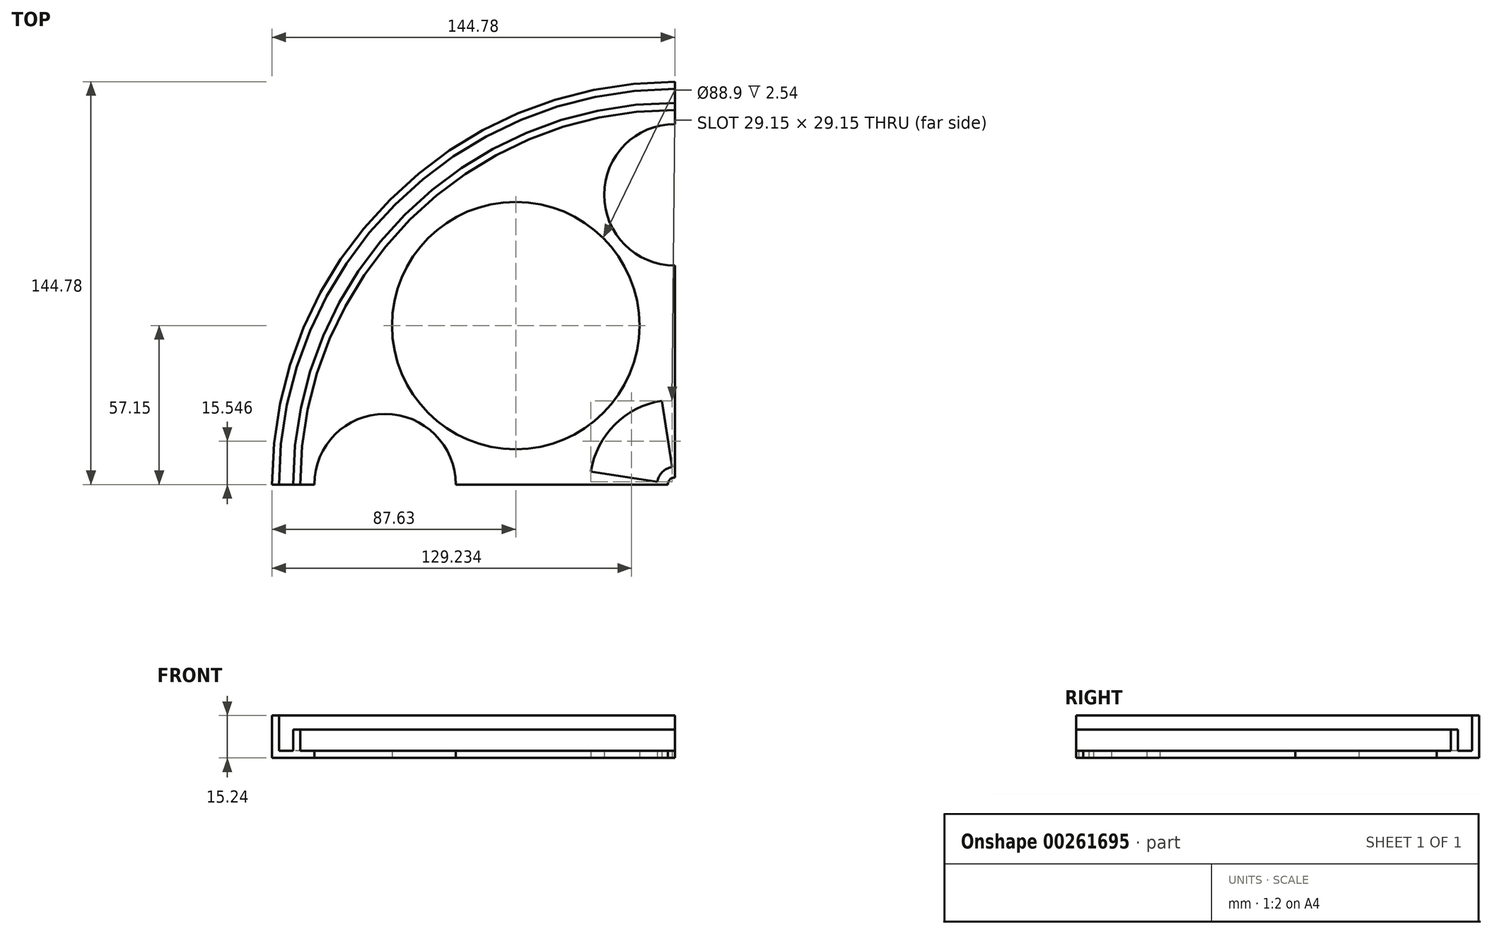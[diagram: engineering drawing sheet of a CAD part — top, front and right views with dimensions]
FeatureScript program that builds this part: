
annotation { "Feature Type Name" : "Feature", "Feature Type Description" : "" }
export const myFeature = defineFeature(function(context is Context, id is Id, definition is map)
    precondition{}
    {
        {
            var Q0;
            Q0=qCreatedBy(makeId("Top.planeOp"),FACE);
            var sketch = newSketch(context, id + "F0", { "sketchPlane" : qUnion([Q0])});
            skCircle(sketch, "E0", {"center": v(0, 0) * mm, "radius": 134.62 * mm});
            skCircle(sketch, "E1.0", {"center": v(0, 0) * mm, "radius": 137.16 * mm});
            skCircle(sketch, "E2.0", {"center": v(0, 0) * mm, "radius": 144.78 * mm});
            skCircle(sketch, "E3.0", {"center": v(0, 0) * mm, "radius": 142.24 * mm});
            skCircle(sketch, "E4.0", {"center": v(0, 0) * mm, "radius": 2.54 * mm});
            skLineSegment(sketch, "E5", {"start": v(0, 0) * mm, "end": v(0, -147.32) * mm});
            skLineSegment(sketch, "E6", {"start": v(-11.57, -144.32) * mm, "end": v(0, -147.32) * mm});
            skFitSpline(sketch, "E7", {"points": [v(0, -147.32) * mm, v(5.92, -144.66) * mm], "startDerivative": vector(10.02, -2.47) * mm, "endDerivative": vector(12.8, 0.33) * mm});
            skLineSegment(sketch, "E8", {"start": v(-8.6, -141.98) * mm, "end": v(0, -144.78) * mm});
            skFitSpline(sketch, "E9", {"points": [v(0, -144.78) * mm, v(4.46, -142.17) * mm], "startDerivative": vector(6.28, -2.02) * mm, "endDerivative": vector(5.88, 0.14) * mm});
            skLineSegment(sketch, "E10", {"start": v(0, 0) * mm, "end": v(-144.78, 0) * mm});
            skLineSegment(sketch, "E11", {"start": v(0, 0) * mm, "end": v(0, 144.78) * mm});
            skLineSegment(sketch, "E12", {"start": v(0, 0) * mm, "end": v(144.78, 0) * mm});
            skLineSegment(sketch, "E13", {"start": v(0, -12.7) * mm, "end": v(-144.22, -12.7) * mm});
            skLineSegment(sketch, "E14", {"start": v(0, -12.7) * mm, "end": v(144.78, -12.7) * mm});
            skLineSegment(sketch, "E15", {"start": v(0, 12.7) * mm, "end": v(-144.22, 12.7) * mm});
            skLineSegment(sketch, "E16", {"start": v(0, 12.7) * mm, "end": v(144.78, 12.7) * mm});
            skLineSegment(sketch, "E17", {"start": v(-12.7, 0) * mm, "end": v(-12.7, 144.22) * mm});
            skLineSegment(sketch, "E18", {"start": v(12.7, 0) * mm, "end": v(12.7, 144.22) * mm});
            skLineSegment(sketch, "E19", {"start": v(-12.7, 0) * mm, "end": v(-12.7, -144.22) * mm});
            skLineSegment(sketch, "E20", {"start": v(12.7, 0) * mm, "end": v(12.7, -144.22) * mm});
            skCircle(sketch, "E21", {"center": v(-57.15, -57.15) * mm, "radius": 44.45 * mm});
            skCircle(sketch, "E22", {"center": v(57.15, -57.15) * mm, "radius": 44.45 * mm});
            skCircle(sketch, "E23", {"center": v(-57.15, 57.15) * mm, "radius": 44.45 * mm});
            skCircle(sketch, "E24", {"center": v(57.15, 57.15) * mm, "radius": 44.45 * mm});
            skCircle(sketch, "E25", {"center": v(-104.14, 0) * mm, "radius": 25.4 * mm});
            skCircle(sketch, "E26", {"center": v(0, 104.14) * mm, "radius": 25.4 * mm});
            skCircle(sketch, "E27", {"center": v(104.14, 0) * mm, "radius": 25.4 * mm});
            skCircle(sketch, "E28", {"center": v(0, -104.14) * mm, "radius": 25.4 * mm});
            skCircle(sketch, "E29", {"center": v(0, 0) * mm, "radius": 30.48 * mm});
            skLineSegment(sketch, "E30", {"start": v(-12.7, -82.14) * mm, "end": v(0, 0) * mm});
            skLineSegment(sketch, "E31", {"start": v(12.7, -82.14) * mm, "end": v(0, 0) * mm});
            skLineSegment(sketch, "E32", {"start": v(82.14, -12.7) * mm, "end": v(0, 0) * mm});
            skLineSegment(sketch, "E33", {"start": v(82.14, 12.7) * mm, "end": v(0, 0) * mm});
            skLineSegment(sketch, "E34", {"start": v(12.7, 82.14) * mm, "end": v(0, 0) * mm});
            skLineSegment(sketch, "E35", {"start": v(-12.7, 82.14) * mm, "end": v(0, 0) * mm});
            skLineSegment(sketch, "E36", {"start": v(-82.14, -12.7) * mm, "end": v(0, 0) * mm});
            skLineSegment(sketch, "E37", {"start": v(-82.14, 12.7) * mm, "end": v(0, 0) * mm});
            skCircle(sketch, "E38", {"center": v(0, 0) * mm, "radius": 6.35 * mm});
            skSolve(sketch);
        }
        {
            var Q0;
            {var subQ0=sQuery(id+"F0.wireOp",EDGE,"E17");var subQ5=sQuery(id+"F0.wireOp",EDGE,"E37");var subQ7=makeQuery(id+"F0.imprint","INTERSECT",VERTEX,{"derivedFrom":[subQ0,subQ5]});Q0=makeQuery(id+"F0.imprint","IMPRINT",FACE,{"disambiguationData":[TD([[makeQuery(id+"F0.imprint","IMPRINT",EDGE,{"disambiguationData":[TD([[subQ7,-1.0]])],"derivedFrom":subQ5}),-1.0]])]});}
            var Q1;
            {var subQ0=sQuery(id+"F0.wireOp",EDGE,"E37");var subQ1=sQuery(id+"F0.wireOp",EDGE,"E4.0");var subQ2=makeQuery(id+"F0.imprint","INTERSECT",VERTEX,{"derivedFrom":[subQ1,subQ0]});Q1=makeQuery(id+"F0.imprint","IMPRINT",FACE,{"disambiguationData":[TD([[makeQuery(id+"F0.imprint","IMPRINT",EDGE,{"disambiguationData":[TD([[subQ2,-1.0]])],"derivedFrom":subQ1}),-1.0]])]});}
            var Q2;
            {var subQ0=sQuery(id+"F0.wireOp",EDGE,"E35");var subQ1=sQuery(id+"F0.wireOp",EDGE,"E4.0");var subQ2=makeQuery(id+"F0.imprint","INTERSECT",VERTEX,{"derivedFrom":[subQ1,subQ0]});Q2=makeQuery(id+"F0.imprint","IMPRINT",FACE,{"disambiguationData":[TD([[makeQuery(id+"F0.imprint","IMPRINT",EDGE,{"disambiguationData":[TD([[subQ2,-1.0]])],"derivedFrom":subQ1}),-1.0]])]});}
            var Q3;
            {var subQ0=sQuery(id+"F0.wireOp",EDGE,"E11");var subQ1=sQuery(id+"F0.wireOp",EDGE,"E4.0");var subQ2=makeQuery(id+"F0.imprint","INTERSECT",VERTEX,{"derivedFrom":[subQ1,subQ0]});Q3=makeQuery(id+"F0.imprint","IMPRINT",FACE,{"disambiguationData":[TD([[makeQuery(id+"F0.imprint","IMPRINT",EDGE,{"disambiguationData":[TD([[subQ2,-1.0]])],"derivedFrom":subQ1}),-1.0]])]});}
            var Q4;
            {var subQ0=sQuery(id+"F0.wireOp",EDGE,"E15");var subQ5=sQuery(id+"F0.wireOp",EDGE,"E35");var subQ6=makeQuery(id+"F0.imprint","INTERSECT",VERTEX,{"derivedFrom":[subQ0,subQ5]});Q4=makeQuery(id+"F0.imprint","IMPRINT",FACE,{"disambiguationData":[TD([[makeQuery(id+"F0.imprint","IMPRINT",EDGE,{"disambiguationData":[TD([[subQ6,-1.0]])],"derivedFrom":subQ5}),1.0]])]});}
            var Q5;
            {var subQ1=sQuery(id+"F0.wireOp",EDGE,"E11");var subQ3=sQuery(id+"F0.wireOp",EDGE,"E29");var subQ4=makeQuery(id+"F0.imprint","INTERSECT",VERTEX,{"derivedFrom":[subQ1,subQ3]});Q5=makeQuery(id+"F0.imprint","IMPRINT",FACE,{"disambiguationData":[TD([[makeQuery(id+"F0.imprint","IMPRINT",EDGE,{"disambiguationData":[TD([[subQ4,-1.0]])],"derivedFrom":subQ3}),1.0]])]});}
            var Q6;
            {var subQ1=sQuery(id+"F0.wireOp",EDGE,"E10");var subQ3=sQuery(id+"F0.wireOp",EDGE,"E29");var subQ4=makeQuery(id+"F0.imprint","INTERSECT",VERTEX,{"derivedFrom":[subQ1,subQ3]});Q6=makeQuery(id+"F0.imprint","IMPRINT",FACE,{"disambiguationData":[TD([[makeQuery(id+"F0.imprint","IMPRINT",EDGE,{"disambiguationData":[TD([[subQ4,1.0]])],"derivedFrom":subQ3}),1.0]])]});}
            var Q7;
            {var subQ0=sQuery(id+"F0.wireOp",EDGE,"E29");var subQ1=sQuery(id+"F0.wireOp",EDGE,"E10");var subQ2=makeQuery(id+"F0.imprint","INTERSECT",VERTEX,{"derivedFrom":[subQ1,subQ0]});Q7=makeQuery(id+"F0.imprint","IMPRINT",FACE,{"disambiguationData":[TD([[makeQuery(id+"F0.imprint","IMPRINT",EDGE,{"disambiguationData":[TD([[subQ2,-1.0]])],"derivedFrom":subQ1}),-1.0]])]});}
            var Q8;
            {var subQ1=sQuery(id+"F0.wireOp",EDGE,"E17");var subQ9=sQuery(id+"F0.wireOp",EDGE,"E0");var subQ10=makeQuery(id+"F0.imprint","INTERSECT",VERTEX,{"derivedFrom":[subQ9,subQ1]});Q8=makeQuery(id+"F0.imprint","IMPRINT",FACE,{"disambiguationData":[TD([[makeQuery(id+"F0.imprint","IMPRINT",EDGE,{"disambiguationData":[TD([[subQ10,-1.0]])],"derivedFrom":subQ9}),1.0]])]});}
            var Q9;
            {var subQ0=sQuery(id+"F0.wireOp",EDGE,"E15");var subQ1=sQuery(id+"F0.wireOp",EDGE,"E0");var subQ2=makeQuery(id+"F0.imprint","INTERSECT",VERTEX,{"derivedFrom":[subQ1,subQ0]});Q9=makeQuery(id+"F0.imprint","IMPRINT",FACE,{"disambiguationData":[TD([[makeQuery(id+"F0.imprint","IMPRINT",EDGE,{"disambiguationData":[TD([[subQ2,-1.0]])],"derivedFrom":subQ1}),1.0]])]});}
            var Q10;
            {var subQ0=sQuery(id+"F0.wireOp",EDGE,"E29");var subQ1=sQuery(id+"F0.wireOp",EDGE,"E15");var subQ2=makeQuery(id+"F0.imprint","INTERSECT",VERTEX,{"derivedFrom":[subQ1,subQ0]});Q10=makeQuery(id+"F0.imprint","IMPRINT",FACE,{"disambiguationData":[TD([[makeQuery(id+"F0.imprint","IMPRINT",EDGE,{"disambiguationData":[TD([[subQ2,-1.0]])],"derivedFrom":subQ1}),1.0]])]});}
            var Q11;
            {var subQ0=sQuery(id+"F0.wireOp",EDGE,"E29");var subQ1=sQuery(id+"F0.wireOp",EDGE,"E15");var subQ2=makeQuery(id+"F0.imprint","INTERSECT",VERTEX,{"derivedFrom":[subQ1,subQ0]});Q11=makeQuery(id+"F0.imprint","IMPRINT",FACE,{"disambiguationData":[TD([[makeQuery(id+"F0.imprint","IMPRINT",EDGE,{"disambiguationData":[TD([[subQ2,-1.0]])],"derivedFrom":subQ1}),-1.0]])]});}
            var Q12;
            {var subQ0=sQuery(id+"F0.wireOp",EDGE,"E29");var subQ1=sQuery(id+"F0.wireOp",EDGE,"E17");var subQ2=makeQuery(id+"F0.imprint","INTERSECT",VERTEX,{"derivedFrom":[subQ1,subQ0]});Q12=makeQuery(id+"F0.imprint","IMPRINT",FACE,{"disambiguationData":[TD([[makeQuery(id+"F0.imprint","IMPRINT",EDGE,{"disambiguationData":[TD([[subQ2,-1.0]])],"derivedFrom":subQ1}),-1.0]])]});}
            var Q13;
            {var subQ0=sQuery(id+"F0.wireOp",EDGE,"E29");var subQ1=sQuery(id+"F0.wireOp",EDGE,"E11");var subQ2=makeQuery(id+"F0.imprint","INTERSECT",VERTEX,{"derivedFrom":[subQ1,subQ0]});Q13=makeQuery(id+"F0.imprint","IMPRINT",FACE,{"disambiguationData":[TD([[makeQuery(id+"F0.imprint","IMPRINT",EDGE,{"disambiguationData":[TD([[subQ2,-1.0]])],"derivedFrom":subQ1}),1.0]])]});}
            var Q14;
            {var subQ0=sQuery(id+"F0.wireOp",EDGE,"E11");var subQ1=sQuery(id+"F0.wireOp",EDGE,"E0");var subQ2=makeQuery(id+"F0.imprint","INTERSECT",VERTEX,{"derivedFrom":[subQ1,subQ0]});Q14=makeQuery(id+"F0.imprint","IMPRINT",FACE,{"disambiguationData":[TD([[makeQuery(id+"F0.imprint","IMPRINT",EDGE,{"disambiguationData":[TD([[subQ2,-1.0]])],"derivedFrom":subQ1}),1.0]])]});}
            extrude(context, id + "F1", {"entities" : qUnion([Q0, Q1, Q2, Q3, Q4, Q5, Q6, Q7, Q8, Q9, Q10, Q11, Q12, Q13, Q14]), "offsetDistance" : 25.4 * mm, "depth" : 2.54 * mm});
        }
        {
            var Q0;
            {var subQ0=sQuery(id+"F0.wireOp",EDGE,"E15");var subQ1=sQuery(id+"F0.wireOp",EDGE,"E0");var subQ2=makeQuery(id+"F0.imprint","INTERSECT",VERTEX,{"derivedFrom":[subQ1,subQ0]});Q0=makeQuery(id+"F0.imprint","IMPRINT",FACE,{"disambiguationData":[TD([[makeQuery(id+"F0.imprint","IMPRINT",EDGE,{"disambiguationData":[TD([[subQ2,-1.0]])],"derivedFrom":subQ1}),-1.0]])]});}
            var Q1;
            {var subQ0=sQuery(id+"F0.wireOp",EDGE,"E17");var subQ1=sQuery(id+"F0.wireOp",EDGE,"E0");var subQ2=makeQuery(id+"F0.imprint","INTERSECT",VERTEX,{"derivedFrom":[subQ1,subQ0]});Q1=makeQuery(id+"F0.imprint","IMPRINT",FACE,{"disambiguationData":[TD([[makeQuery(id+"F0.imprint","IMPRINT",EDGE,{"disambiguationData":[TD([[subQ2,-1.0]])],"derivedFrom":subQ1}),-1.0]])]});}
            var Q2;
            {var subQ0=sQuery(id+"F0.wireOp",EDGE,"E11");var subQ1=sQuery(id+"F0.wireOp",EDGE,"E0");var subQ2=makeQuery(id+"F0.imprint","INTERSECT",VERTEX,{"derivedFrom":[subQ1,subQ0]});Q2=makeQuery(id+"F0.imprint","IMPRINT",FACE,{"disambiguationData":[TD([[makeQuery(id+"F0.imprint","IMPRINT",EDGE,{"disambiguationData":[TD([[subQ2,-1.0]])],"derivedFrom":subQ1}),-1.0]])]});}
            extrude(context, id + "F2", {"entities" : qUnion([Q0, Q1, Q2]), "operationType" : NewBodyOperationType.ADD, "offsetDistance" : 25.4 * mm, "depth" : 7.62 * mm});
        }
        {
            var Q0;
            {var subQ0=sQuery(id+"F0.wireOp",EDGE,"E15");var subQ1=sQuery(id+"F0.wireOp",EDGE,"E1.0");var subQ2=makeQuery(id+"F0.imprint","INTERSECT",VERTEX,{"derivedFrom":[subQ1,subQ0]});Q0=makeQuery(id+"F0.imprint","IMPRINT",FACE,{"disambiguationData":[TD([[makeQuery(id+"F0.imprint","IMPRINT",EDGE,{"disambiguationData":[TD([[subQ2,-1.0]])],"derivedFrom":subQ1}),-1.0]])]});}
            var Q1;
            {var subQ0=sQuery(id+"F0.wireOp",EDGE,"E17");var subQ1=sQuery(id+"F0.wireOp",EDGE,"E1.0");var subQ2=makeQuery(id+"F0.imprint","INTERSECT",VERTEX,{"derivedFrom":[subQ1,subQ0]});Q1=makeQuery(id+"F0.imprint","IMPRINT",FACE,{"disambiguationData":[TD([[makeQuery(id+"F0.imprint","IMPRINT",EDGE,{"disambiguationData":[TD([[subQ2,-1.0]])],"derivedFrom":subQ1}),-1.0]])]});}
            var Q2;
            Q2=makeQuery(id+"F2.opExtrude","CAP_FACE",FACE,{"disambiguationData":[OSD([sQuery(id+"F0.wireOp",EDGE,"E0"),sQuery(id+"F0.wireOp",EDGE,"E1.0"),sQuery(id+"F0.wireOp",EDGE,"E5"),sQuery(id+"F0.wireOp",EDGE,"E19")])],"isStart":false});
            var Q3;
            {var subQ0=sQuery(id+"F0.wireOp",EDGE,"E11");var subQ1=sQuery(id+"F0.wireOp",EDGE,"E1.0");var subQ2=makeQuery(id+"F0.imprint","INTERSECT",VERTEX,{"derivedFrom":[subQ1,subQ0]});Q3=makeQuery(id+"F0.imprint","IMPRINT",FACE,{"disambiguationData":[TD([[makeQuery(id+"F0.imprint","IMPRINT",EDGE,{"disambiguationData":[TD([[subQ2,-1.0]])],"derivedFrom":subQ1}),-1.0]])]});}
            extrude(context, id + "F3", {"entities" : qUnion([Q0, Q1, Q2, Q3]), "operationType" : NewBodyOperationType.ADD, "offsetDistance" : 25.4 * mm, "depth" : 2.54 * mm});
        }
        {
            var Q0;
            {var subQ0=sQuery(id+"F0.wireOp",EDGE,"E10");var subQ1=sQuery(id+"F0.wireOp",EDGE,"E2.0");var subQ2=makeQuery(id+"F0.imprint","INTERSECT",VERTEX,{"derivedFrom":[subQ1,subQ0]});Q0=makeQuery(id+"F0.imprint","IMPRINT",FACE,{"disambiguationData":[TD([[makeQuery(id+"F0.imprint","IMPRINT",EDGE,{"disambiguationData":[TD([[subQ2,1.0]])],"derivedFrom":subQ1}),1.0]])]});}
            var Q1;
            {var subQ0=sQuery(id+"F0.wireOp",EDGE,"E15");var subQ1=sQuery(id+"F0.wireOp",EDGE,"E2.0");var subQ2=makeQuery(id+"F0.imprint","INTERSECT",VERTEX,{"derivedFrom":[subQ1,subQ0]});Q1=makeQuery(id+"F0.imprint","IMPRINT",FACE,{"disambiguationData":[TD([[makeQuery(id+"F0.imprint","IMPRINT",EDGE,{"disambiguationData":[TD([[subQ2,1.0]])],"derivedFrom":subQ1}),1.0]])]});}
            var Q2;
            {var subQ0=sQuery(id+"F0.wireOp",EDGE,"E11");var subQ1=sQuery(id+"F0.wireOp",EDGE,"E2.0");var subQ2=makeQuery(id+"F0.imprint","INTERSECT",VERTEX,{"derivedFrom":[subQ1,subQ0]});Q2=makeQuery(id+"F0.imprint","IMPRINT",FACE,{"disambiguationData":[TD([[makeQuery(id+"F0.imprint","IMPRINT",EDGE,{"disambiguationData":[TD([[subQ2,-1.0]])],"derivedFrom":subQ1}),1.0]])]});}
            extrude(context, id + "F4", {"entities" : qUnion([Q0, Q1, Q2]), "operationType" : NewBodyOperationType.ADD, "offsetDistance" : 25.4 * mm, "depth" : 15.24 * mm});
        }
    });
